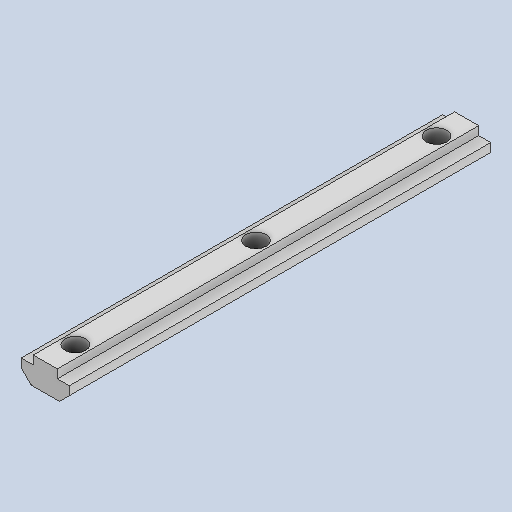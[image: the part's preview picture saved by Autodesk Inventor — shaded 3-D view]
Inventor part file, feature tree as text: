
AUTODESK INVENTOR PART (.ipt)
format: ipt  version: 2022 (Build 260153000, 153)  size: 93,184 bytes
history: native  units: in
note: dims shown in document units (in); Inventor stores cm internally (conversion verified against a paired STEP export)
features: hole x1
ambient origin geometry x8: Origin, YZ Plane, XZ Plane, XY Plane, X Axis, Y Axis, Z Axis, Center Point
bodies: Solid1 (feature_tree)
feature tree (1):
  hole  "Hole2"  [1 undecoded]
note: 1 required parameter value undecoded (feature->parameter linkage not recoverable at this tier; creation-order binding heuristic only, values carry confidence <= 0.55)
